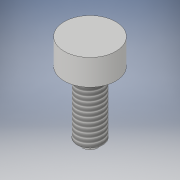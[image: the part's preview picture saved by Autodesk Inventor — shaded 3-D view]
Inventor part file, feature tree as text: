
AUTODESK INVENTOR PART (.ipt)
format: ipt  version: 2018 (Build 220112000, 112)  size: 110,592 bytes
history: native  units: in
note: dims shown in document units (in); Inventor stores cm internally (conversion verified against a paired STEP export)
features: revolve x1, chamfer x1, thread x1, sketch x1
ambient origin geometry x8: Origin, YZ Plane, XZ Plane, XY Plane, X Axis, Y Axis, Z Axis, Center Point
bodies: Solid1 (feature_tree)
feature tree (4):
  revolve  "Revolution1"  [1 undecoded]
  chamfer  "Chamfer1"  Distance=0.3937in
  thread  "Thread1"  [1 undecoded]
  sketch  "Sketch2"  dims[d3=1.4173in d6=0.3937in d7=0.3937in d8=0.1969in d9=90.0deg d10=0.0787in d11=0.0787in d12=45.0deg d13=0.3937in d14=0.0in]
note: 2 required parameter values undecoded (feature->parameter linkage not recoverable at this tier; creation-order binding heuristic only, values carry confidence <= 0.55)